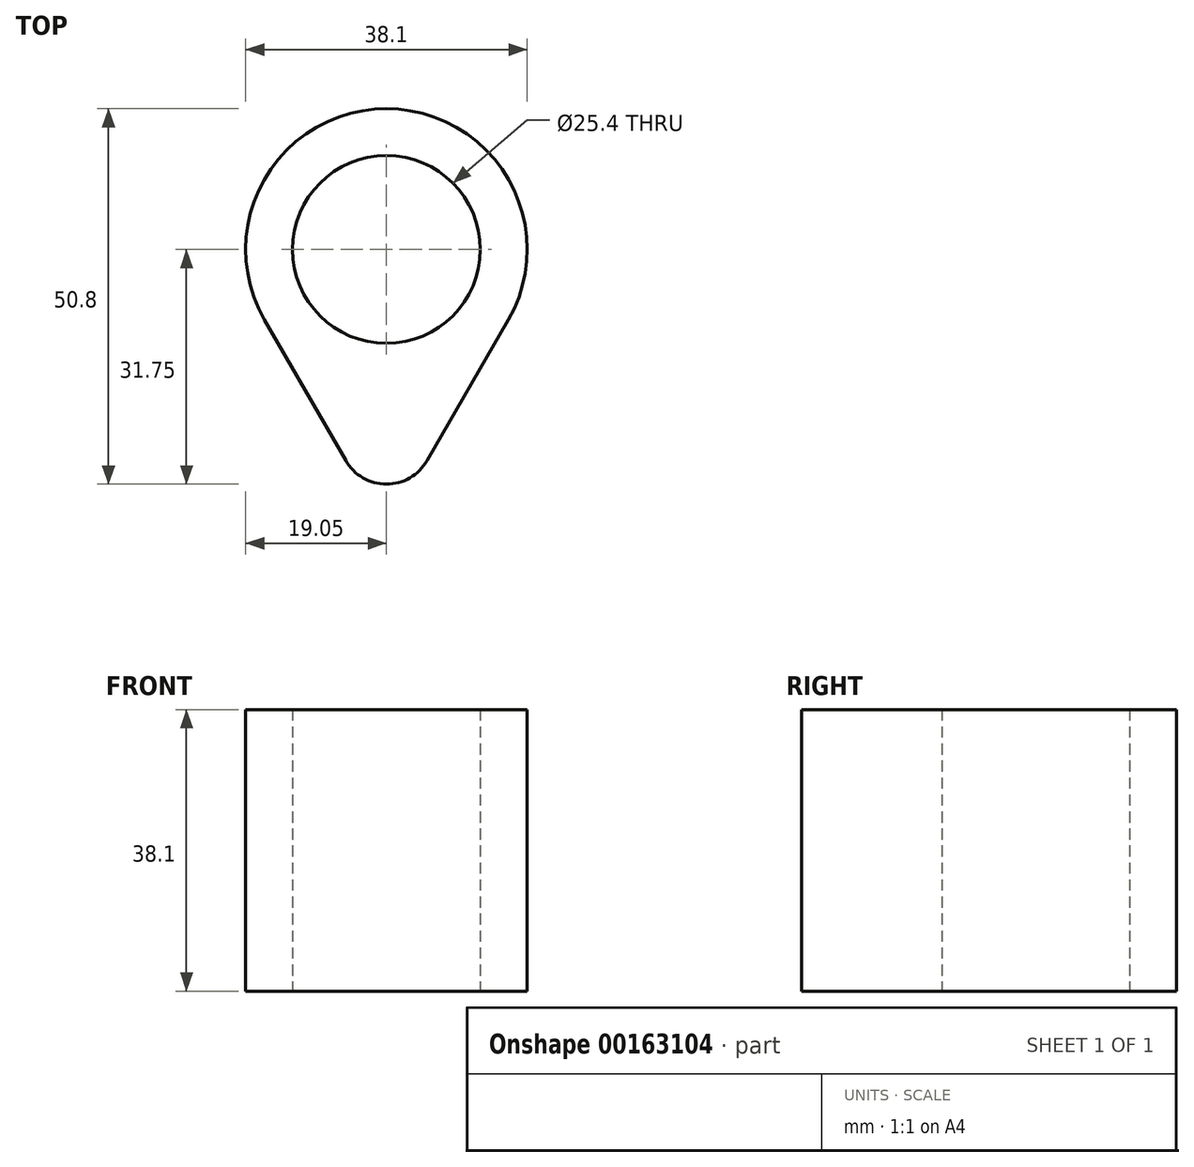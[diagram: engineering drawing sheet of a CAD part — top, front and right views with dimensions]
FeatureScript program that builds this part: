
annotation { "Feature Type Name" : "Feature", "Feature Type Description" : "" }
export const myFeature = defineFeature(function(context is Context, id is Id, definition is map)
    precondition{}
    {
        {
            var Q0;
            Q0=qCreatedBy(makeId("Top.planeOp"),FACE);
            var sketch = newSketch(context, id + "F0", { "sketchPlane" : qUnion([Q0])});
            skCircle(sketch, "E0", {"center": v(0, 0) * mm, "radius": 12.7 * mm});
            skArc(sketch, "E1", {"start": v(16.5, -9.53) * mm, "mid": v(0, 19.05) * mm, "end": v(-16.5, -9.52) * mm});
            skArc(sketch, "E2", {"start": v(-5.5, -28.58) * mm, "mid": v(0, -31.75) * mm, "end": v(5.5, -28.58) * mm});
            skLineSegment(sketch, "E3", {"start": v(-16.5, -9.53) * mm, "end": v(-5.5, -28.58) * mm});
            skLineSegment(sketch, "E4", {"start": v(16.5, -9.53) * mm, "end": v(5.5, -28.58) * mm});
            skSolve(sketch);
        }
        {
            var Q0;
            Q0=makeQuery(id+"F0.imprint","IMPRINT",FACE,{"disambiguationData":[TD([[makeQuery(id+"F0.imprint","IMPRINT",EDGE,{"derivedFrom":sQuery(id+"F0.wireOp",EDGE,"E0")}),-1.0]])]});
            extrude(context, id + "F1", {"entities" : qUnion([Q0]), "depth" : 38.1 * mm});
        }
    });
